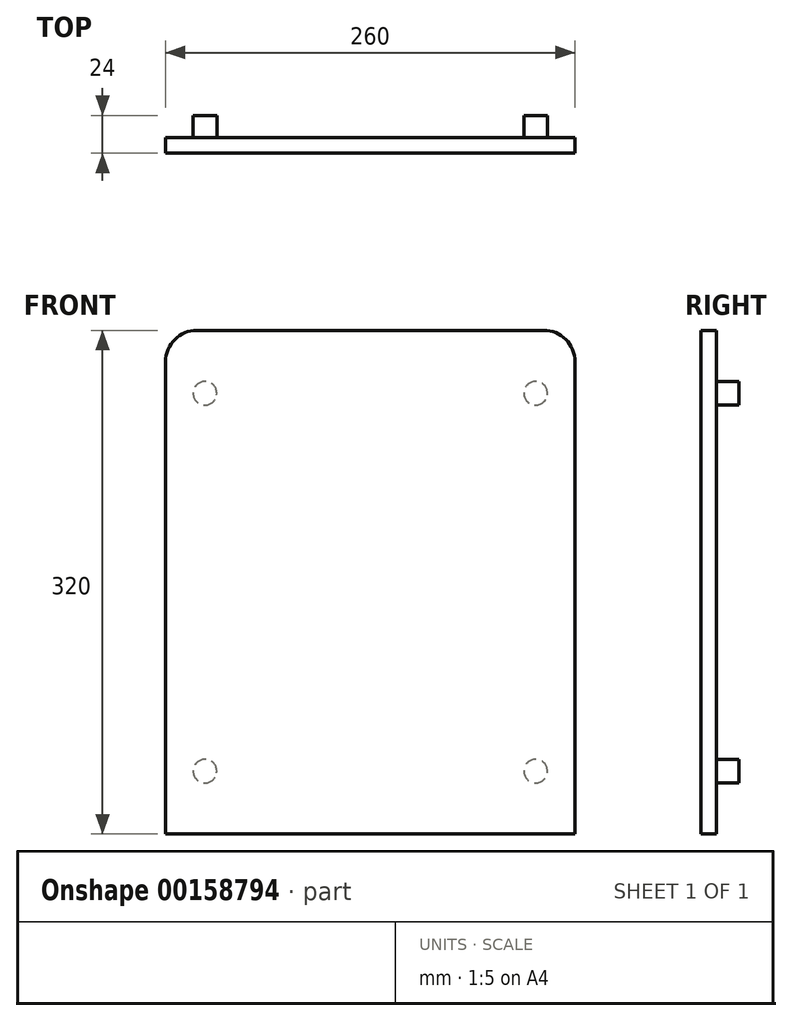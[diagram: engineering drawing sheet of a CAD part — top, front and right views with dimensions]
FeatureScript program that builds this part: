
annotation { "Feature Type Name" : "Feature", "Feature Type Description" : "" }
export const myFeature = defineFeature(function(context is Context, id is Id, definition is map)
    precondition{}
    {
        {
            var Q0;
            Q0=qCreatedBy(makeId("Front.planeOp"),FACE);
            var sketch = newSketch(context, id + "F0", { "sketchPlane" : qUnion([Q0])});
            skLineSegment(sketch, "E0.bottom", {"start": v(130, 160) * mm, "end": v(-130, 160) * mm});
            skLineSegment(sketch, "E0.top", {"start": v(130, -160) * mm, "end": v(-130, -160) * mm});
            skLineSegment(sketch, "E0.left", {"start": v(130, 160) * mm, "end": v(130, -160) * mm});
            skLineSegment(sketch, "E0.right", {"start": v(-130, 160) * mm, "end": v(-130, -160) * mm});
            skPoint(sketch, "E0.middle", {"position": v(0, 0) * mm});
            skSolve(sketch);
        }
        {
            var Q0;
            Q0 = qSketchRegion(id + "F0", true);
            extrude(context, id + "F1", {"entities" : qUnion([Q0]), "depth" : 10 * mm});
        }
        {
            var Q0;
            Q0=makeQuery(id+"F1.opExtrude","SWEPT_EDGE",EDGE,{"disambiguationData":[OSD([sQuery(id+"F0.wireOp",EDGE,"E0.bottom"),sQuery(id+"F0.wireOp",EDGE,"E0.right")])]});
            var Q1;
            Q1=makeQuery(id+"F1.opExtrude","SWEPT_EDGE",EDGE,{"disambiguationData":[OSD([sQuery(id+"F0.wireOp",EDGE,"E0.bottom"),sQuery(id+"F0.wireOp",EDGE,"E0.left")])]});
            fillet(context, id + "F2", {"entities" : qUnion([Q0, Q1]), "radius" : 20 * mm, "tangentPropagation" : true, "allowEdgeOverflow" : false});
        }
        {
            var Q0;
            Q0=makeQuery(id+"F1.opExtrude","CAP_FACE",FACE,{"disambiguationData":[OSD([sQuery(id+"F0.wireOp",EDGE,"E0.bottom"),sQuery(id+"F0.wireOp",EDGE,"E0.top"),sQuery(id+"F0.wireOp",EDGE,"E0.left"),sQuery(id+"F0.wireOp",EDGE,"E0.right")])],"isStart":true});
            var sketch = newSketch(context, id + "F3", { "sketchPlane" : qUnion([Q0])});
            skLineSegment(sketch, "E1.top", {"start": v(-130, -120) * mm, "end": v(-105, -120) * mm});
            skCircle(sketch, "E2", {"center": v(-105, -120) * mm, "radius": 7.5 * mm});
            skLineSegment(sketch, "E3.top", {"start": v(130, -120) * mm, "end": v(105, -120) * mm});
            skCircle(sketch, "E4", {"center": v(105, -120) * mm, "radius": 7.5 * mm});
            skLineSegment(sketch, "E5.top", {"start": v(130, 120) * mm, "end": v(105, 120) * mm});
            skCircle(sketch, "E6", {"center": v(105, 120) * mm, "radius": 7.5 * mm});
            skLineSegment(sketch, "E7.top", {"start": v(-130, 120) * mm, "end": v(-105, 120) * mm});
            skCircle(sketch, "E8", {"center": v(-105, 120) * mm, "radius": 7.5 * mm});
            skLineSegment(sketch, "E9", {"start": v(-105, 120) * mm, "end": v(-105, 160) * mm});
            skLineSegment(sketch, "E10", {"start": v(-105, -120) * mm, "end": v(-105, -160) * mm});
            skLineSegment(sketch, "E11", {"start": v(105, -120) * mm, "end": v(105, -160) * mm});
            skLineSegment(sketch, "E12", {"start": v(105, 120) * mm, "end": v(105, 160) * mm});
            skSolve(sketch);
        }
        {
            var Q0;
            Q0 = qSketchRegion(id + "F3", true);
            extrude(context, id + "F4", {"entities" : qUnion([Q0]), "operationType" : NewBodyOperationType.ADD, "depth" : 14 * mm});
        }
    });
